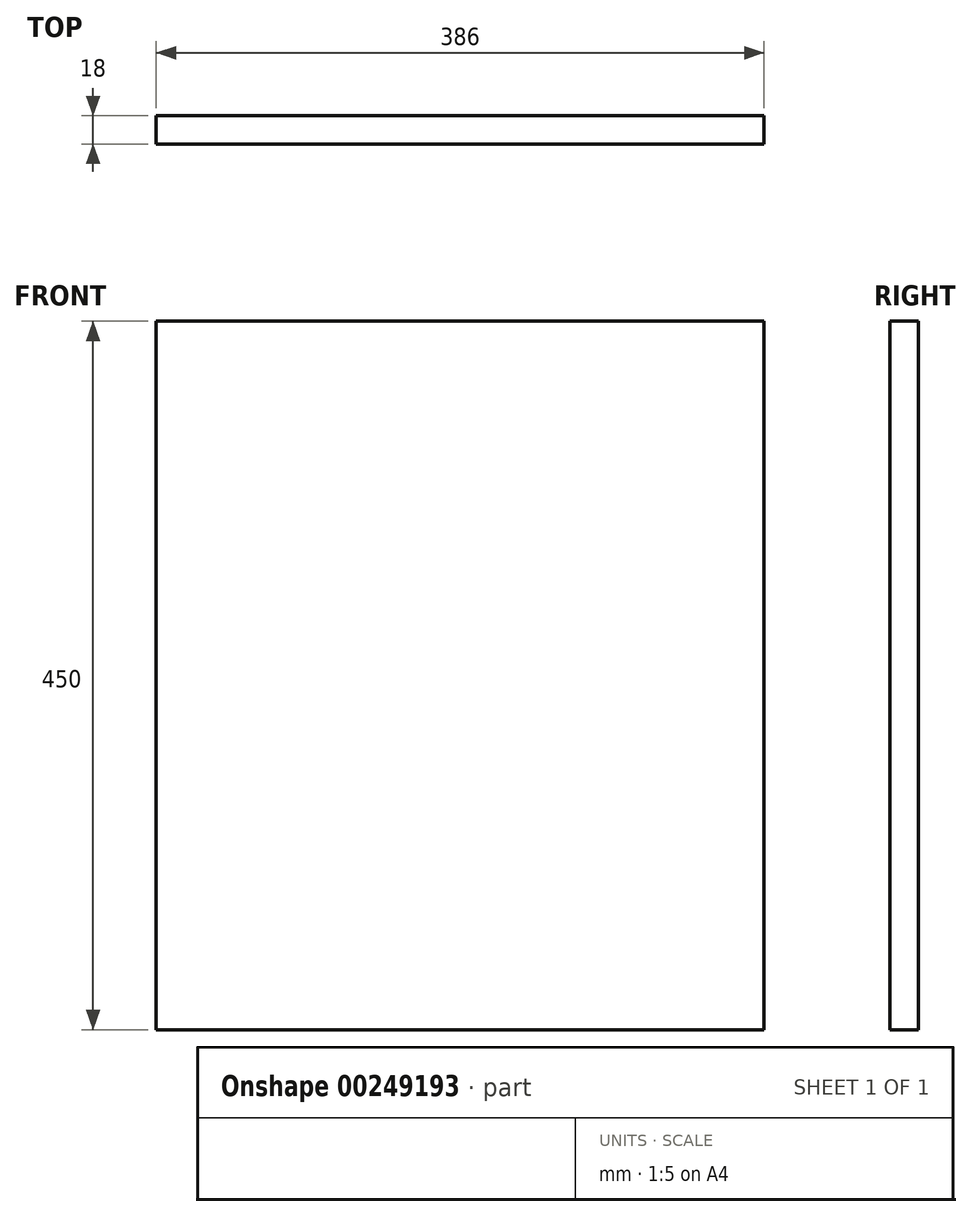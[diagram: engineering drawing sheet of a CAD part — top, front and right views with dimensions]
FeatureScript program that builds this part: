
annotation { "Feature Type Name" : "Feature", "Feature Type Description" : "" }
export const myFeature = defineFeature(function(context is Context, id is Id, definition is map)
    precondition{}
    {
        {
            var Q0;
            Q0=qCreatedBy(makeId("Front.planeOp"),FACE);
            var sketch = newSketch(context, id + "F0", { "sketchPlane" : qUnion([Q0])});
            skLineSegment(sketch, "E0.bottom", {"start": v(193, 225) * mm, "end": v(-193, 225) * mm});
            skLineSegment(sketch, "E0.top", {"start": v(193, -225) * mm, "end": v(-193, -225) * mm});
            skLineSegment(sketch, "E0.left", {"start": v(193, 225) * mm, "end": v(193, -225) * mm});
            skLineSegment(sketch, "E0.right", {"start": v(-193, 225) * mm, "end": v(-193, -225) * mm});
            skPoint(sketch, "E0.middle", {"position": v(0, 0) * mm});
            skSolve(sketch);
        }
        {
            var Q0;
            Q0 = qSketchRegion(id + "F0", true);
            extrude(context, id + "F1", {"entities" : qUnion([Q0]), "depth" : 18 * mm});
        }
    });
